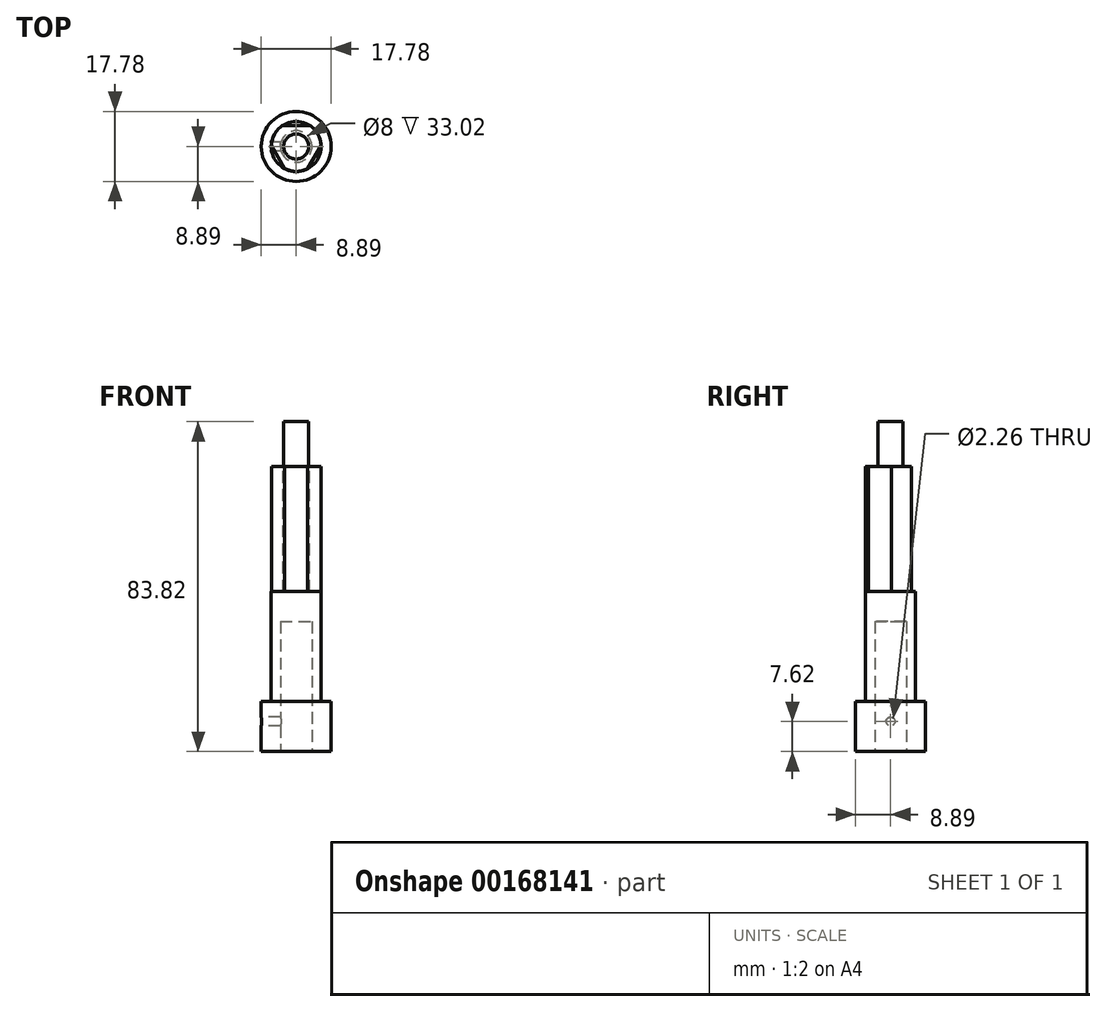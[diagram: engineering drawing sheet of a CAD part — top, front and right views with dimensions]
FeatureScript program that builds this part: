
annotation { "Feature Type Name" : "Feature", "Feature Type Description" : "" }
export const myFeature = defineFeature(function(context is Context, id is Id, definition is map)
    precondition{}
    {
        {
            var Q0;
            Q0=qCreatedBy(makeId("Top.planeOp"),FACE);
            var sketch = newSketch(context, id + "F0", { "sketchPlane" : qUnion([Q0])});
            skCircle(sketch, "E0", {"center": v(0, 0) * mm, "radius": 8.9 * mm});
            skSolve(sketch);
        }
        {
            var Q0;
            Q0=makeQuery(id+"F0.imprint","IMPRINT",FACE,{"disambiguationData":[TD([[makeQuery(id+"F0.imprint","IMPRINT",EDGE,{"derivedFrom":sQuery(id+"F0.wireOp",EDGE,"E0")}),1.0]])]});
            extrude(context, id + "F1", {"entities" : qUnion([Q0]), "depth" : 12.7 * mm});
        }
        {
            var Q0;
            Q0=makeQuery(id+"F1.opExtrude","CAP_FACE",FACE,{"disambiguationData":[OSD([sQuery(id+"F0.wireOp",EDGE,"E0")])],"isStart":false});
            var sketch = newSketch(context, id + "F2", { "sketchPlane" : qUnion([Q0])});
            skCircle(sketch, "E1", {"center": v(0, 0) * mm, "radius": 6.35 * mm});
            skSolve(sketch);
        }
        {
            var Q0;
            Q0=qSketchRegion(id+"F2",true);
            extrude(context, id + "F3", {"entities" : qUnion([Q0]), "operationType" : NewBodyOperationType.ADD, "depth" : 27.94 * mm});
        }
        {
            var Q0;
            Q0=makeQuery(id+"F3.opExtrude","CAP_FACE",FACE,{"disambiguationData":[OSD([sQuery(id+"F2.wireOp",EDGE,"E1")])],"isStart":false});
            var sketch = newSketch(context, id + "F4", { "sketchPlane" : qUnion([Q0])});
            skCircle(sketch, "E2.cCircle", {"center": v(0, 0) * mm, "radius": 5.33 * mm, "construction": true});
            skLineSegment(sketch, "E2.0", {"start": v(9.24, 5.33) * mm, "end": v(0, -10.67) * mm});
            skLineSegment(sketch, "E2.1", {"start": v(0, -10.67) * mm, "end": v(-9.24, 5.33) * mm});
            skLineSegment(sketch, "E2.2", {"start": v(-9.24, 5.33) * mm, "end": v(9.24, 5.33) * mm});
            skPoint(sketch, "E2.0.midPoint", {"position": v(4.62, -2.67) * mm});
            skSolve(sketch);
        }
        {
            var Q0;
            Q0=qSketchRegion(id+"F4",true);
            extrude(context, id + "F5", {"entities" : qUnion([Q0]), "operationType" : NewBodyOperationType.ADD, "depth" : 43.18 * mm});
        }
        {
            var Q0;
            Q0=makeQuery(id+"F5.opExtrude","CAP_FACE",FACE,{"disambiguationData":[OSD([sQuery(id+"F4.wireOp",EDGE,"E2.0"),sQuery(id+"F4.wireOp",EDGE,"E2.1"),sQuery(id+"F4.wireOp",EDGE,"E2.2")])],"isStart":false});
            var sketch = newSketch(context, id + "F6", { "sketchPlane" : qUnion([Q0])});
            skCircle(sketch, "E3", {"center": v(0, 0) * mm, "radius": 6.32 * mm});
            skCircle(sketch, "E4", {"center": v(0, 0) * mm, "radius": 20.25 * mm});
            skSolve(sketch);
        }
        {
            var Q0;
            Q0 = qSketchRegion(id + "F6", true);
            var Q1;
            {var subQ0=sQuery(id+"F2.wireOp",EDGE,"E1");var subQ1=sQuery(id+"F4.wireOp",EDGE,"E2.0");Q1=makeQuery(id+"F5.boolean.opBoolean","SPLIT",FACE,{"disambiguationData":[TD([makeQuery(id+"F5.opExtrude","SWEPT_FACE",FACE,{"disambiguationData":[OSD([subQ1])]})])],"derivedFrom":makeQuery(id+"F3.opExtrude","CAP_FACE",FACE,{"disambiguationData":[OSD([subQ0])],"isStart":false})});}
            extrude(context, id + "F7", {"entities" : qUnion([Q0]), "operationType" : NewBodyOperationType.REMOVE, "endBound" : BoundingType.UP_TO_SURFACE, "oppositeDirection" : true, "endBoundEntityFace" : qUnion([Q1]), "depth" : 25.4 * mm});
        }
        {
            var Q0;
            Q0=makeQuery(id+"F1.opExtrude","CAP_FACE",FACE,{"disambiguationData":[OSD([sQuery(id+"F0.wireOp",EDGE,"E0")])],"isStart":true});
            var sketch = newSketch(context, id + "F8", { "sketchPlane" : qUnion([Q0])});
            skCircle(sketch, "E5", {"center": v(0, 0) * mm, "radius": 4 * mm});
            skSolve(sketch);
        }
        {
            var Q0;
            Q0=makeQuery(id+"F8.imprint","IMPRINT",FACE,{"disambiguationData":[TD([[makeQuery(id+"F8.imprint","IMPRINT",EDGE,{"derivedFrom":sQuery(id+"F8.wireOp",EDGE,"E5")}),1.0]])]});
            extrude(context, id + "F9", {"entities" : qUnion([Q0]), "operationType" : NewBodyOperationType.REMOVE, "oppositeDirection" : true, "depth" : 33.02 * mm});
        }
        {
            var Q0;
            Q0=makeQuery(id+"F1.opExtrude","CAP_FACE",FACE,{"disambiguationData":[OSD([sQuery(id+"F0.wireOp",EDGE,"E0")])],"isStart":false});
            var sketch = newSketch(context, id + "F10", { "sketchPlane" : qUnion([Q0])});
            skCircle(sketch, "E6.0", {"center": v(0, 0) * mm, "radius": 8.9 * mm, "construction": true});
            skPoint(sketch, "E7", {"position": v(-8.9, 0) * mm});
            skSolve(sketch);
        }
        {
            var Q0;
            Q0=sQuery(id+"F10.wireOp",VERTEX,"E7");
            var Q1;
            Q1=qCreatedBy(makeId("Right.planeOp"),FACE);
            cPlane(context, id + "F11", {"entities" : qUnion([Q0, Q1]), "cplaneType" : CPlaneType.PLANE_POINT, "offset" : 25.4 * mm, "width" : 152.4 * mm, "height" : 152.4 * mm});
        }
        {
            var Q0;
            Q0=qCreatedBy(id+"F11.planeOp",FACE);
            var sketch = newSketch(context, id + "F12", { "sketchPlane" : qUnion([Q0])});
            skLineSegment(sketch, "E8", {"start": v(0, 0) * mm, "end": v(0, 7.62) * mm, "construction": true});
            skPoint(sketch, "E9", {"position": v(0, 7.62) * mm});
            skSolve(sketch);
        }
        {
            var Q0;
            Q0=sQuery(id+"F12.wireOp",VERTEX,"E9");
            var Q1;
            Q1=makeQuery(id+"F1.opExtrude","SWEPT_BODY",BODY,{"disambiguationData":[OSD([sQuery(id+"F0.wireOp",EDGE,"E0")])]});
            hole(context, id + "F13", {"style" : HoleStyle.SIMPLE, "endStyle" : HoleEndStyle.BLIND, "oppositeDirection" : true, "standardTappedOrClearance" : lookupTablePath({ "standard" : "ANSI", "engagement" : "75%", "pitch" : "40 tpi", "size" : "#4", "type" : "Tapped" }), "standardBlindInLast" : lookupTablePath({ "standard" : "ANSI", "engagement" : "75%", "pitch" : "40 tpi", "size" : "#4", "type" : "Tapped" }), "holeDiameter" : 2.26 * mm, "holeDepth" : 8.9 * mm, "locations" : qUnion([Q0]), "scope" : qUnion([Q1]), "majorDiameter" : 2.84 * mm});
        }
        {
            var Q0;
            Q0=makeQuery(id+"F5.opExtrude","CAP_FACE",FACE,{"disambiguationData":[OSD([sQuery(id+"F4.wireOp",EDGE,"E2.0"),sQuery(id+"F4.wireOp",EDGE,"E2.1"),sQuery(id+"F4.wireOp",EDGE,"E2.2")])],"isStart":false});
            var sketch = newSketch(context, id + "F14", { "sketchPlane" : qUnion([Q0])});
            skCircle(sketch, "E10", {"center": v(0, 0) * mm, "radius": 3.18 * mm});
            skCircle(sketch, "E11", {"center": v(0, 0) * mm, "radius": 8.9 * mm});
            skSolve(sketch);
        }
        {
            var Q0;
            Q0=qSketchRegion(id+"F14",true);
            extrude(context, id + "F15", {"entities" : qUnion([Q0]), "operationType" : NewBodyOperationType.REMOVE, "oppositeDirection" : true, "depth" : 11.43 * mm});
        }
    });
